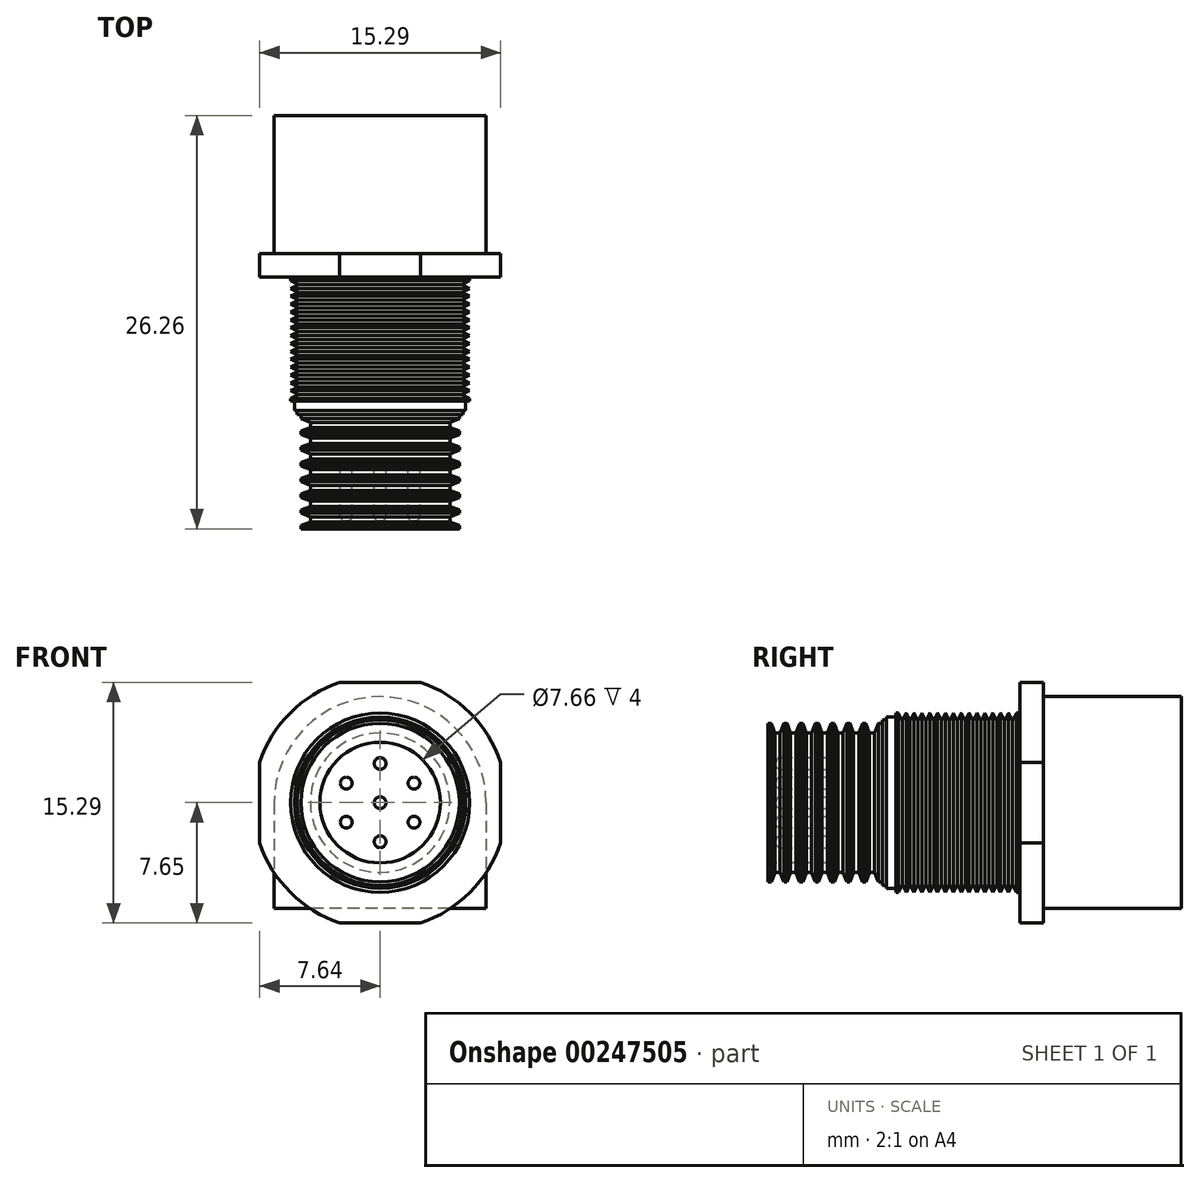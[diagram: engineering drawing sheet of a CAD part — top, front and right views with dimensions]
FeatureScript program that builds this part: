
annotation { "Feature Type Name" : "Feature", "Feature Type Description" : "" }
export const myFeature = defineFeature(function(context is Context, id is Id, definition is map)
    precondition{}
    {
        {
            var Q0;
            Q0=qCreatedBy(makeId("Front.planeOp"),FACE);
            var sketch = newSketch(context, id + "F0", { "sketchPlane" : qUnion([Q0])});
            skArc(sketch, "E0", {"start": v(-2.57, 7.64) * mm, "mid": v(-5.7, 5.7) * mm, "end": v(-7.64, 2.57) * mm});
            skLineSegment(sketch, "E1.bottom", {"start": v(2.57, -7.64) * mm, "end": v(-2.57, -7.65) * mm});
            skLineSegment(sketch, "E1.top", {"start": v(2.57, 7.64) * mm, "end": v(-2.57, 7.64) * mm});
            skLineSegment(sketch, "E1.left", {"start": v(7.64, -2.57) * mm, "end": v(7.64, 2.57) * mm});
            skLineSegment(sketch, "E1.right", {"start": v(-7.64, -2.57) * mm, "end": v(-7.64, 2.57) * mm});
            skPoint(sketch, "E2.orphan", {"position": v(7.64, 7.65) * mm});
            skArc(sketch, "E3.trimOffspring", {"start": v(7.64, 2.57) * mm, "mid": v(5.7, 5.7) * mm, "end": v(2.57, 7.65) * mm});
            skPoint(sketch, "E4.orphan", {"position": v(-7.65, 7.64) * mm});
            skArc(sketch, "E5.trimOffspring", {"start": v(-7.64, -2.57) * mm, "mid": v(-5.7, -5.7) * mm, "end": v(-2.57, -7.65) * mm});
            skPoint(sketch, "E6.orphan", {"position": v(-7.64, -7.65) * mm});
            skArc(sketch, "E7.trimOffspring", {"start": v(2.57, -7.64) * mm, "mid": v(5.7, -5.7) * mm, "end": v(7.65, -2.57) * mm});
            skPoint(sketch, "E8.orphan", {"position": v(7.65, -7.64) * mm});
            skSolve(sketch);
        }
        {
            var Q0;
            Q0=qSketchRegion(id+"F0",true);
            extrude(context, id + "F1", {"entities" : qUnion([Q0]), "depth" : 1.5 * mm});
        }
        {
            var Q0;
            Q0=makeQuery(id+"F1.opExtrude","CAP_FACE",FACE,{"disambiguationData":[OSD([sQuery(id+"F0.wireOp",EDGE,"E0"),sQuery(id+"F0.wireOp",EDGE,"E1.bottom"),sQuery(id+"F0.wireOp",EDGE,"E1.top"),sQuery(id+"F0.wireOp",EDGE,"E1.left"),sQuery(id+"F0.wireOp",EDGE,"E1.right"),sQuery(id+"F0.wireOp",EDGE,"E3.trimOffspring"),sQuery(id+"F0.wireOp",EDGE,"E5.trimOffspring"),sQuery(id+"F0.wireOp",EDGE,"E7.trimOffspring")])],"isStart":true});
            var sketch = newSketch(context, id + "F2", { "sketchPlane" : qUnion([Q0])});
            skArc(sketch, "E9", {"start": v(6.73, 0) * mm, "mid": v(0, 6.73) * mm, "end": v(-6.73, 0) * mm});
            skLineSegment(sketch, "E10.top", {"start": v(-6.73, -6.73) * mm, "end": v(6.73, -6.73) * mm});
            skLineSegment(sketch, "E10.left", {"start": v(-6.73, 0) * mm, "end": v(-6.73, -6.73) * mm});
            skLineSegment(sketch, "E10.right", {"start": v(6.73, 0) * mm, "end": v(6.73, -6.73) * mm});
            skSolve(sketch);
        }
        {
            var Q0;
            Q0=qSketchRegion(id+"F2",true);
            extrude(context, id + "F3", {"entities" : qUnion([Q0]), "operationType" : NewBodyOperationType.ADD, "depth" : 8.76 * mm});
        }
        {
            var Q0;
            Q0=qCreatedBy(makeId("Right.planeOp"),FACE);
            var sketch = newSketch(context, id + "F4", { "sketchPlane" : qUnion([Q0])});
            skLineSegment(sketch, "E11.top", {"start": v(-1.5, 0) * mm, "end": v(-9.5, 0) * mm});
            skLineSegment(sketch, "E11.left", {"start": v(-1.5, 5.69) * mm, "end": v(-1.5, 0) * mm});
            skLineSegment(sketch, "E12.0.1", {"start": v(-1.5, 7.64) * mm, "end": v(-1.5, 2.57) * mm});
            skLineSegment(sketch, "E12.0.2", {"start": v(-1.5, 2.57) * mm, "end": v(-1.5, -2.57) * mm});
            skLineSegment(sketch, "E12.0.3", {"start": v(-1.5, -2.57) * mm, "end": v(-1.5, -7.65) * mm});
            skLineSegment(sketch, "E12.0.5", {"start": v(-1.5, -7.64) * mm, "end": v(-1.5, -2.57) * mm});
            skLineSegment(sketch, "E12.0.6", {"start": v(-1.5, -2.57) * mm, "end": v(-1.5, 2.57) * mm});
            skLineSegment(sketch, "E12.0.7", {"start": v(-1.5, 2.57) * mm, "end": v(-1.5, 7.65) * mm});
            skLineSegment(sketch, "E13", {"start": v(0, 0) * mm, "end": v(-25.59, 0) * mm, "construction": true});
            skPoint(sketch, "E13.endSnap0", {"position": v(-1.5, 0) * mm});
            skLineSegment(sketch, "E14", {"start": v(-9.23, 5.7) * mm, "end": v(-8.98, 5.2) * mm});
            skLineSegment(sketch, "E15", {"start": v(-8.98, 5.2) * mm, "end": v(-8.73, 5.7) * mm});
            skLineSegment(sketch, "E16.1.0.0", {"start": v(-8.73, 5.69) * mm, "end": v(-8.48, 5.2) * mm});
            skLineSegment(sketch, "E16.1.0.1", {"start": v(-8.48, 5.2) * mm, "end": v(-8.23, 5.7) * mm});
            skLineSegment(sketch, "E16.2.0.0", {"start": v(-8.23, 5.7) * mm, "end": v(-7.98, 5.2) * mm});
            skLineSegment(sketch, "E16.2.0.1", {"start": v(-7.98, 5.2) * mm, "end": v(-7.73, 5.7) * mm});
            skLineSegment(sketch, "E16.3.0.0", {"start": v(-7.73, 5.7) * mm, "end": v(-7.48, 5.2) * mm});
            skLineSegment(sketch, "E16.3.0.1", {"start": v(-7.48, 5.2) * mm, "end": v(-7.23, 5.7) * mm});
            skLineSegment(sketch, "E16.4.0.0", {"start": v(-7.23, 5.7) * mm, "end": v(-6.98, 5.2) * mm});
            skLineSegment(sketch, "E16.4.0.1", {"start": v(-6.98, 5.2) * mm, "end": v(-6.73, 5.7) * mm});
            skLineSegment(sketch, "E16.5.0.0", {"start": v(-6.73, 5.7) * mm, "end": v(-6.48, 5.2) * mm});
            skLineSegment(sketch, "E16.5.0.1", {"start": v(-6.48, 5.2) * mm, "end": v(-6.23, 5.7) * mm});
            skLineSegment(sketch, "E16.6.0.0", {"start": v(-6.23, 5.7) * mm, "end": v(-5.98, 5.2) * mm});
            skLineSegment(sketch, "E16.6.0.1", {"start": v(-5.98, 5.2) * mm, "end": v(-5.73, 5.7) * mm});
            skLineSegment(sketch, "E16.7.0.0", {"start": v(-5.73, 5.7) * mm, "end": v(-5.48, 5.2) * mm});
            skLineSegment(sketch, "E16.7.0.1", {"start": v(-5.48, 5.2) * mm, "end": v(-5.23, 5.7) * mm});
            skLineSegment(sketch, "E16.8.0.0", {"start": v(-5.23, 5.7) * mm, "end": v(-4.98, 5.2) * mm});
            skLineSegment(sketch, "E16.8.0.1", {"start": v(-4.98, 5.2) * mm, "end": v(-4.73, 5.7) * mm});
            skLineSegment(sketch, "E16.9.0.0", {"start": v(-4.73, 5.7) * mm, "end": v(-4.48, 5.2) * mm});
            skLineSegment(sketch, "E16.9.0.1", {"start": v(-4.48, 5.2) * mm, "end": v(-4.23, 5.7) * mm});
            skLineSegment(sketch, "E16.10.0.0", {"start": v(-4.23, 5.7) * mm, "end": v(-3.98, 5.2) * mm});
            skLineSegment(sketch, "E16.10.0.1", {"start": v(-3.98, 5.2) * mm, "end": v(-3.73, 5.7) * mm});
            skLineSegment(sketch, "E16.11.0.0", {"start": v(-3.73, 5.7) * mm, "end": v(-3.48, 5.2) * mm});
            skLineSegment(sketch, "E16.11.0.1", {"start": v(-3.48, 5.2) * mm, "end": v(-3.23, 5.7) * mm});
            skLineSegment(sketch, "E16.direction1", {"start": v(-8.98, 5.19) * mm, "end": v(-8.48, 5.19) * mm, "construction": true});
            skLineSegment(sketch, "E17.0.12.0", {"start": v(-3.23, 5.7) * mm, "end": v(-2.98, 5.2) * mm});
            skLineSegment(sketch, "E17.3.12.0", {"start": v(-2.98, 5.2) * mm, "end": v(-2.73, 5.7) * mm});
            skLineSegment(sketch, "E17.0.13.0", {"start": v(-2.73, 5.7) * mm, "end": v(-2.48, 5.2) * mm});
            skLineSegment(sketch, "E17.3.13.0", {"start": v(-2.48, 5.2) * mm, "end": v(-2.23, 5.7) * mm});
            skLineSegment(sketch, "E18.0.14.0", {"start": v(-2.23, 5.7) * mm, "end": v(-1.98, 5.2) * mm});
            skLineSegment(sketch, "E18.3.14.0", {"start": v(-1.98, 5.2) * mm, "end": v(-1.73, 5.7) * mm});
            skLineSegment(sketch, "E19", {"start": v(-1.73, 5.7) * mm, "end": v(-1.5, 5.7) * mm});
            skLineSegment(sketch, "E20", {"start": v(-9.39, 5.44) * mm, "end": v(-9.98, 5.44) * mm});
            skLineSegment(sketch, "E21", {"start": v(-9.98, 5.44) * mm, "end": v(-9.98, 5.26) * mm});
            skLineSegment(sketch, "E22", {"start": v(-9.98, 5.26) * mm, "end": v(-10.24, 5.26) * mm});
            skLineSegment(sketch, "E23", {"start": v(-10.24, 5.26) * mm, "end": v(-10.24, 5.03) * mm});
            skLineSegment(sketch, "E24", {"start": v(-10.33, 0) * mm, "end": v(-9.5, 0) * mm});
            skPoint(sketch, "E25.orphan", {"position": v(-9.1, 5.44) * mm});
            skLineSegment(sketch, "E26", {"start": v(-9.23, 5.7) * mm, "end": v(-9.39, 5.7) * mm});
            skLineSegment(sketch, "E27", {"start": v(-9.39, 5.69) * mm, "end": v(-9.39, 5.44) * mm});
            skLineSegment(sketch, "E28", {"start": v(-17.5, 5.03) * mm, "end": v(-17.5, 0) * mm});
            skLineSegment(sketch, "E29", {"start": v(-17.5, 0) * mm, "end": v(-10.33, 0) * mm});
            skLineSegment(sketch, "E30", {"start": v(-10.5, 5.03) * mm, "end": v(-10.74, 4.43) * mm});
            skLineSegment(sketch, "E31", {"start": v(-10.74, 4.43) * mm, "end": v(-11.07, 4.43) * mm});
            skLineSegment(sketch, "E32", {"start": v(-11.07, 4.43) * mm, "end": v(-11.29, 5.03) * mm});
            skLineSegment(sketch, "E33", {"start": v(-11.29, 5.03) * mm, "end": v(-11.5, 5.03) * mm});
            skLineSegment(sketch, "E34", {"start": v(-10.5, 5.03) * mm, "end": v(-10.24, 5.03) * mm});
            skLineSegment(sketch, "E35.1.0.0", {"start": v(-12.29, 5.03) * mm, "end": v(-12.5, 5.03) * mm});
            skLineSegment(sketch, "E35.1.0.1", {"start": v(-12.07, 4.43) * mm, "end": v(-12.29, 5.03) * mm});
            skLineSegment(sketch, "E35.1.0.2", {"start": v(-11.74, 4.43) * mm, "end": v(-12.07, 4.43) * mm});
            skLineSegment(sketch, "E35.1.0.3", {"start": v(-11.5, 5.03) * mm, "end": v(-11.74, 4.43) * mm});
            skLineSegment(sketch, "E35.2.0.0", {"start": v(-13.29, 5.03) * mm, "end": v(-13.5, 5.03) * mm});
            skLineSegment(sketch, "E35.2.0.1", {"start": v(-13.07, 4.43) * mm, "end": v(-13.29, 5.03) * mm});
            skLineSegment(sketch, "E35.2.0.2", {"start": v(-12.74, 4.43) * mm, "end": v(-13.07, 4.43) * mm});
            skLineSegment(sketch, "E35.2.0.3", {"start": v(-12.5, 5.03) * mm, "end": v(-12.74, 4.43) * mm});
            skLineSegment(sketch, "E35.3.0.0", {"start": v(-14.29, 5.03) * mm, "end": v(-14.5, 5.03) * mm});
            skLineSegment(sketch, "E35.3.0.1", {"start": v(-14.07, 4.43) * mm, "end": v(-14.29, 5.03) * mm});
            skLineSegment(sketch, "E35.3.0.2", {"start": v(-13.74, 4.43) * mm, "end": v(-14.07, 4.43) * mm});
            skLineSegment(sketch, "E35.3.0.3", {"start": v(-13.5, 5.03) * mm, "end": v(-13.74, 4.43) * mm});
            skLineSegment(sketch, "E35.4.0.0", {"start": v(-15.29, 5.03) * mm, "end": v(-15.5, 5.03) * mm});
            skLineSegment(sketch, "E35.4.0.1", {"start": v(-15.07, 4.43) * mm, "end": v(-15.29, 5.03) * mm});
            skLineSegment(sketch, "E35.4.0.2", {"start": v(-14.74, 4.43) * mm, "end": v(-15.07, 4.43) * mm});
            skLineSegment(sketch, "E35.4.0.3", {"start": v(-14.5, 5.03) * mm, "end": v(-14.74, 4.43) * mm});
            skLineSegment(sketch, "E35.5.0.0", {"start": v(-16.29, 5.03) * mm, "end": v(-16.5, 5.03) * mm});
            skLineSegment(sketch, "E35.5.0.1", {"start": v(-16.07, 4.43) * mm, "end": v(-16.29, 5.03) * mm});
            skLineSegment(sketch, "E35.5.0.2", {"start": v(-15.74, 4.43) * mm, "end": v(-16.07, 4.43) * mm});
            skLineSegment(sketch, "E35.5.0.3", {"start": v(-15.5, 5.03) * mm, "end": v(-15.74, 4.43) * mm});
            skLineSegment(sketch, "E35.6.0.0", {"start": v(-17.29, 5.03) * mm, "end": v(-17.5, 5.03) * mm});
            skLineSegment(sketch, "E35.6.0.1", {"start": v(-17.07, 4.43) * mm, "end": v(-17.29, 5.03) * mm});
            skLineSegment(sketch, "E35.6.0.2", {"start": v(-16.74, 4.43) * mm, "end": v(-17.07, 4.43) * mm});
            skLineSegment(sketch, "E35.6.0.3", {"start": v(-16.5, 5.03) * mm, "end": v(-16.74, 4.43) * mm});
            skLineSegment(sketch, "E35.direction1", {"start": v(-11.5, 5.03) * mm, "end": v(-12.5, 5.03) * mm, "construction": true});
            skSolve(sketch);
        }
        {
            var Q0;
            Q0=qSketchRegion(id+"F4",true);
            var Q1;
            Q1=sQuery(id+"F4.wireOp",EDGE,"E13");
            revolve(context, id + "F5", {"operationType" : NewBodyOperationType.ADD, "entities" : qUnion([Q0]), "axis" : qUnion([Q1]), "revolveType" : RevolveType.FULL});
        }
        {
            var Q0;
            Q0=makeQuery(id+"F5.opRevolve","SWEPT_FACE",FACE,{"disambiguationData":[OSD([sQuery(id+"F4.wireOp",EDGE,"E28")])]});
            var sketch = newSketch(context, id + "F6", { "sketchPlane" : qUnion([Q0])});
            skCircle(sketch, "E36", {"center": v(0, 0) * mm, "radius": 3.83 * mm});
            skSolve(sketch);
        }
        {
            var Q0;
            Q0=qSketchRegion(id+"F6",true);
            extrude(context, id + "F7", {"entities" : qUnion([Q0]), "operationType" : NewBodyOperationType.REMOVE, "oppositeDirection" : true, "depth" : 4 * mm});
        }
        {
            var Q0;
            Q0=makeQuery(id+"F7.boolean.opBoolean","COPY",FACE,{"derivedFrom":makeQuery(id+"F7.opExtrude","CAP_FACE",FACE,{"disambiguationData":[OSD([sQuery(id+"F6.wireOp",EDGE,"E36")])],"isStart":false})});
            var sketch = newSketch(context, id + "F8", { "sketchPlane" : qUnion([Q0])});
            skCircle(sketch, "E37", {"center": v(0, 0) * mm, "radius": 0.38 * mm});
            skCircle(sketch, "E38", {"center": v(0, 0) * mm, "radius": 2.49 * mm, "construction": true});
            skCircle(sketch, "E39", {"center": v(0, 2.49) * mm, "radius": 0.38 * mm});
            skCircle(sketch, "E40.1.0", {"center": v(-2.15, 1.24) * mm, "radius": 0.38 * mm});
            skCircle(sketch, "E40.2.0", {"center": v(-2.15, -1.24) * mm, "radius": 0.38 * mm});
            skCircle(sketch, "E40.3.0", {"center": v(0, -2.49) * mm, "radius": 0.38 * mm});
            skCircle(sketch, "E40.4.0", {"center": v(2.15, -1.24) * mm, "radius": 0.38 * mm});
            skCircle(sketch, "E40.5.0", {"center": v(2.15, 1.24) * mm, "radius": 0.38 * mm});
            skSolve(sketch);
        }
        {
            var Q0;
            Q0=qSketchRegion(id+"F8",true);
            extrude(context, id + "F9", {"entities" : qUnion([Q0]), "depth" : 3.5 * mm});
        }
        {
            var Q0;
            Q0=makeQuery(id+"F9.opExtrude","CAP_EDGE",EDGE,{"disambiguationData":[OSD([sQuery(id+"F8.wireOp",EDGE,"E40.1.0")])],"isStart":false});
            fillet(context, id + "F10", {"entities" : qUnion([Q0]), "radius" : .3 * mm, "tangentPropagation" : true, "allowEdgeOverflow" : false});
        }
        {
            var Q0;
            Q0=makeQuery(id+"F9.opExtrude","CAP_EDGE",EDGE,{"disambiguationData":[OSD([sQuery(id+"F8.wireOp",EDGE,"E39")])],"isStart":false});
            var Q1;
            Q1=makeQuery(id+"F9.opExtrude","CAP_EDGE",EDGE,{"disambiguationData":[OSD([sQuery(id+"F8.wireOp",EDGE,"E40.5.0")])],"isStart":false});
            var Q2;
            Q2=makeQuery(id+"F9.opExtrude","CAP_EDGE",EDGE,{"disambiguationData":[OSD([sQuery(id+"F8.wireOp",EDGE,"E37")])],"isStart":false});
            var Q3;
            Q3=makeQuery(id+"F9.opExtrude","CAP_EDGE",EDGE,{"disambiguationData":[OSD([sQuery(id+"F8.wireOp",EDGE,"E40.4.0")])],"isStart":false});
            var Q4;
            Q4=makeQuery(id+"F9.opExtrude","CAP_EDGE",EDGE,{"disambiguationData":[OSD([sQuery(id+"F8.wireOp",EDGE,"E40.3.0")])],"isStart":false});
            var Q5;
            Q5=makeQuery(id+"F9.opExtrude","CAP_EDGE",EDGE,{"disambiguationData":[OSD([sQuery(id+"F8.wireOp",EDGE,"E40.2.0")])],"isStart":false});
            fillet(context, id + "F11", {"entities" : qUnion([Q0, Q1, Q2, Q3, Q4, Q5]), "radius" : .3 * mm, "tangentPropagation" : true, "allowEdgeOverflow" : false});
        }
    });
